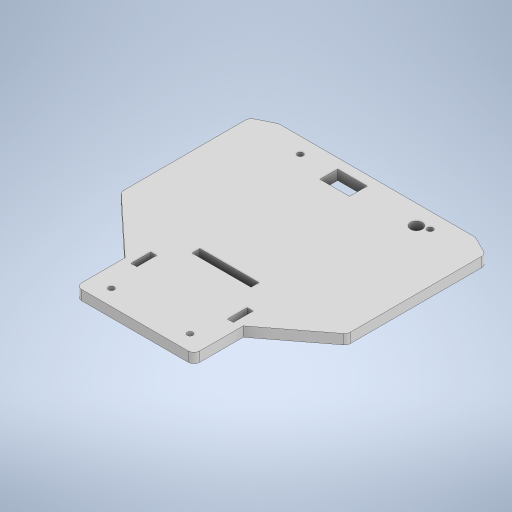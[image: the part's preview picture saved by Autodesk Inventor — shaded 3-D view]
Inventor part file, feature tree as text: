
AUTODESK INVENTOR PART (.ipt)
format: ipt  version: 2023 (Build 270158000, 158)  size: 312,832 bytes
history: native  units: in
note: dims shown in document units (in); Inventor stores cm internally (conversion verified against a paired STEP export)
features: extrude x2, sketch x2, fillet x1
ambient origin geometry x8: Origin, YZ Plane, XZ Plane, XY Plane, X Axis, Y Axis, Z Axis, Center Point
bodies: Solid1 (feature_tree)
feature tree (5):
  extrude  "Extrusion1"  Depth=2.7559in
  fillet  "Fillet1"  Radius=2.7559in
  extrude  "Extrusion2"  Depth=0.7874in
  sketch  "Sketch1"  dims[d0=4.7244in d1=5.9055in d18=2.7559in d43=2.1654in d44=2.7559in]
  sketch  "Sketch2"  dims[d45=1.378in d46=0.7874in d47=1.5748in d48=0.1102in d49=0.1102in d50=0.9843in d51=0.9843in d52=0.1575in d53=0.315in d54=0.1575in d55=0.315in d56=0.1102in d57=0.1102in d58=0.1969in d59=0.0in d60=0.1181in d61=0.3937in d62=1.1811in d63=0.2362in d64=0.1969in d65=90.0deg d68=0.5906in d69=0.3543in d70=0.0in d71=0.0in d73=0.9843in d74=0.9843in d76=2.5591in d77=0.9055in d78=1.811in d79=0.1181in d80=0.7874in d81=0.1181in d82=0.7874in d83=0.3937in d84=0.3937in d85=1.1811in]
